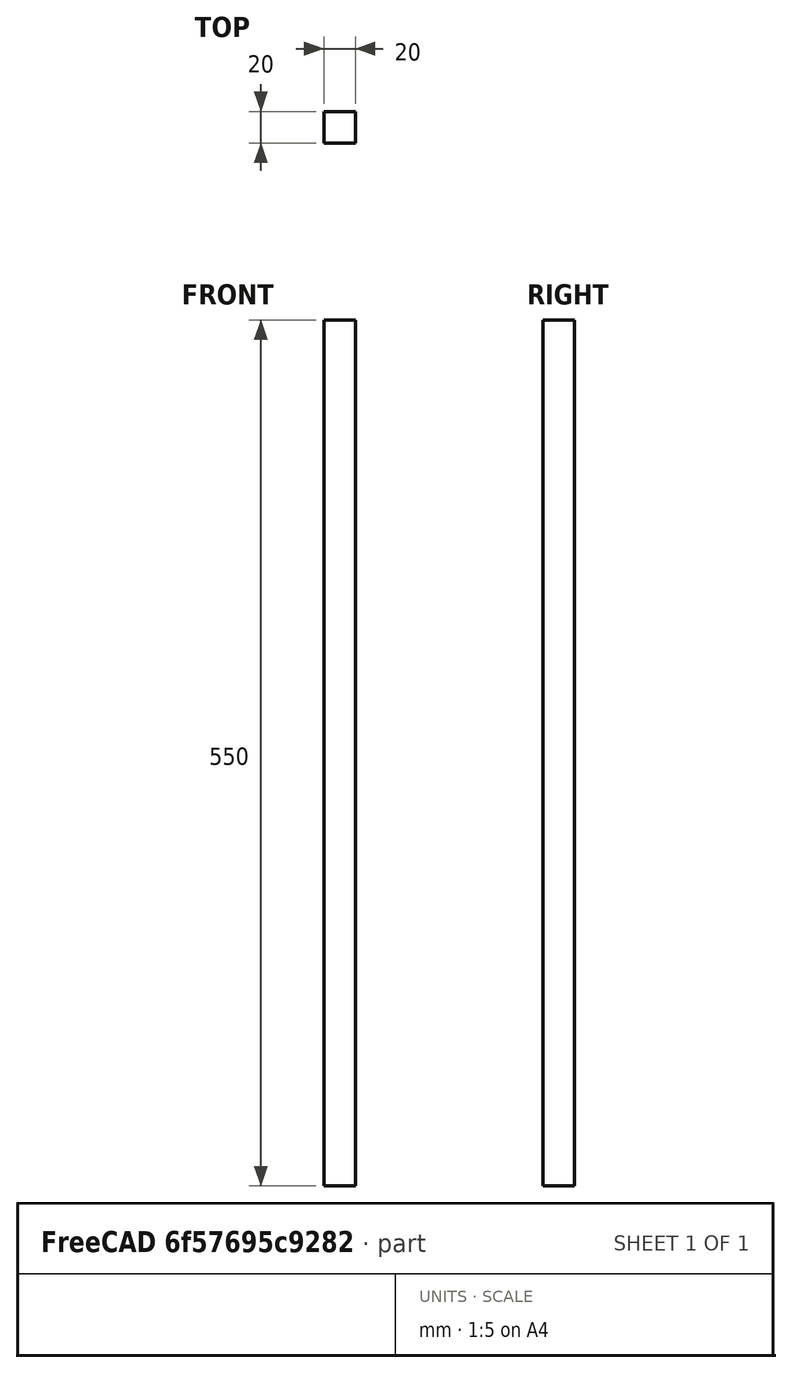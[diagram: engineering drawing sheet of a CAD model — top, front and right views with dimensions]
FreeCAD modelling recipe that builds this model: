
FCSTD DOCUMENT  (FreeCAD 0.19R24276 (Git))
Label: L550
License: All rights reserved
LicenseURL: http://en.wikipedia.org/wiki/All_rights_reserved
objects: Sketcher::SketchObject×1, PartDesign::Pad×1, PartDesign::Body×1
note: 4 computed .brp shape members not serialized (recipe doc carries the construction recipe); baked Part::Feature solids carry a one-line shape summary decoded from their .brp

FEATURE [Sketcher::SketchObject] Sketch
  FullyConstrained = true
  MapMode = 5
  Support = -> [XY_Plane]
  sketch-geometry (4):
    g0: LineSegment StartX=0 StartY=0 StartZ=0 EndX=20 EndY=0 EndZ=0
    g1: LineSegment StartX=20 StartY=0 StartZ=0 EndX=20 EndY=-20 EndZ=0
    g2: LineSegment StartX=20 StartY=-20 StartZ=0 EndX=0 EndY=-20 EndZ=0
    g3: LineSegment StartX=0 StartY=-20 StartZ=0 EndX=0 EndY=0 EndZ=0
  constraints (11):
    c: Coincident(g0,g1)
    c: Coincident(g1,g2)
    c: Coincident(g2,g3)
    c: Coincident(g3,g0)
    c: Horizontal(g0)
    c: Horizontal(g2)
    c: Vertical(g1)
    c: Vertical(g3)
    c: Coincident(g0,g-1)
    c: Equal(g1,g2)
    c: DistanceY(g1,g1) = 20
FEATURE [PartDesign::Pad] Pad
  Direction = (1,1,1)
  Length = 550
  Length2 = 100
  Profile = -> Sketch
  Type = 0
FEATURE [PartDesign::Body] Body
  Group = -> [Sketch,Pad]
  Origin = -> Origin
  Tip = -> Pad
